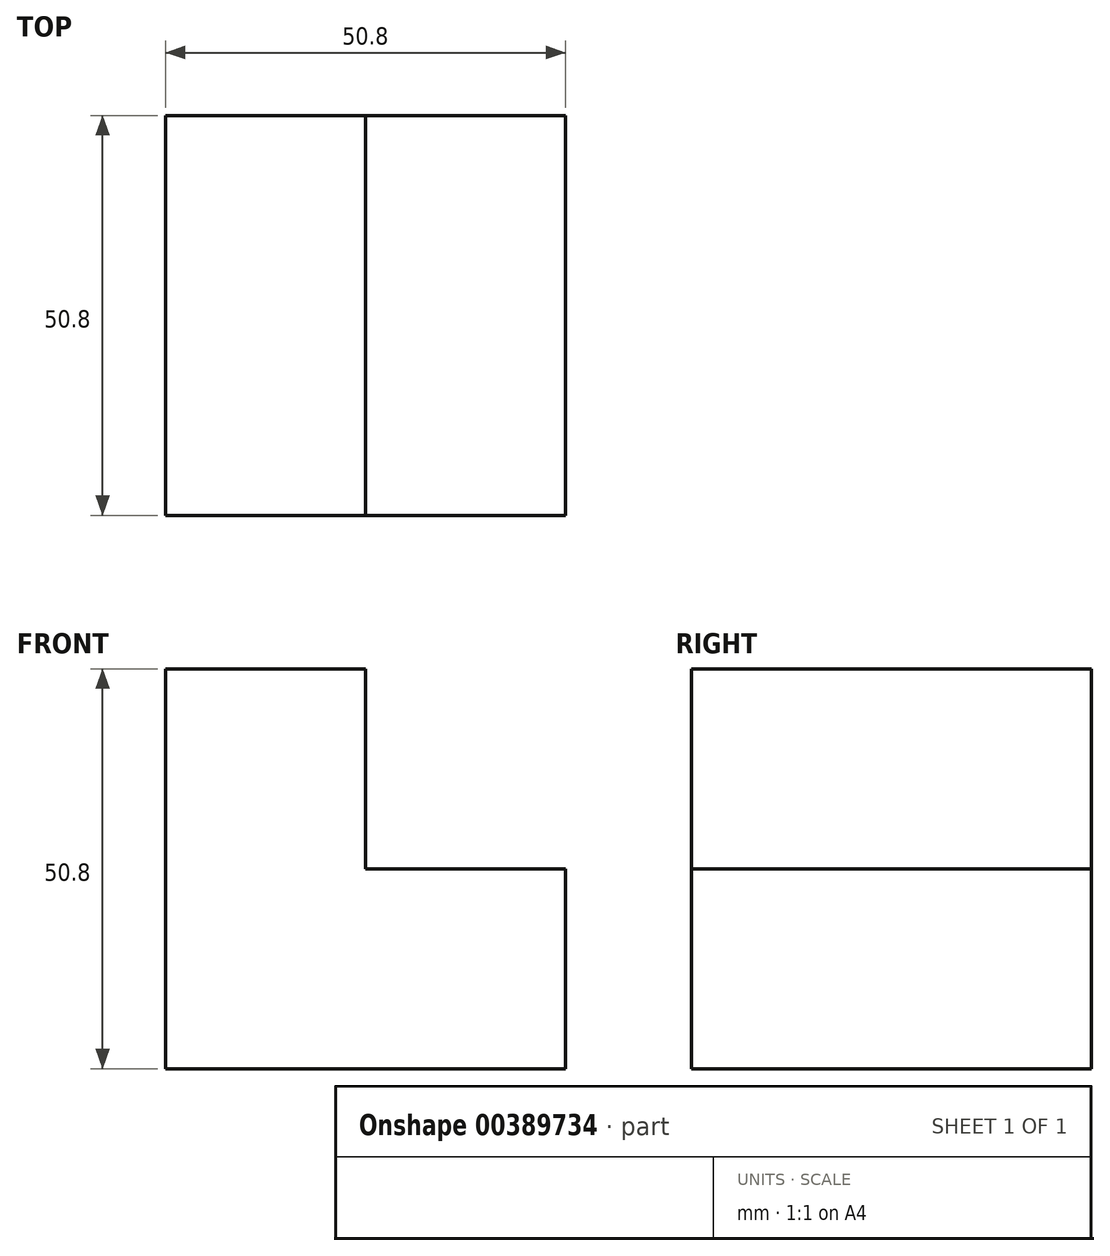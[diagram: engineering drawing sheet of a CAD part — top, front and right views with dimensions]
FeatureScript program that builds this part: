
annotation { "Feature Type Name" : "Feature", "Feature Type Description" : "" }
export const myFeature = defineFeature(function(context is Context, id is Id, definition is map)
    precondition{}
    {
        {
            var Q0;
            Q0=qCreatedBy(makeId("Front.planeOp"),FACE);
            var sketch = newSketch(context, id + "F0", { "sketchPlane" : qUnion([Q0])});
            skLineSegment(sketch, "E0.bottom", {"start": v(0, 0) * mm, "end": v(25.4, 0) * mm});
            skLineSegment(sketch, "E0.top", {"start": v(0, 25.4) * mm, "end": v(25.4, 25.4) * mm});
            skLineSegment(sketch, "E0.left", {"start": v(0, 0) * mm, "end": v(0, 25.4) * mm});
            skLineSegment(sketch, "E0.right", {"start": v(25.4, 0) * mm, "end": v(25.4, 25.4) * mm});
            skLineSegment(sketch, "E1.top", {"start": v(0, 50.8) * mm, "end": v(25.4, 50.8) * mm});
            skLineSegment(sketch, "E1.left", {"start": v(0, 25.4) * mm, "end": v(0, 50.8) * mm});
            skLineSegment(sketch, "E1.right", {"start": v(25.4, 25.4) * mm, "end": v(25.4, 50.8) * mm});
            skLineSegment(sketch, "E2.bottom", {"start": v(25.4, 25.4) * mm, "end": v(50.8, 25.4) * mm});
            skLineSegment(sketch, "E2.top", {"start": v(25.4, 0) * mm, "end": v(50.8, 0) * mm});
            skLineSegment(sketch, "E2.left", {"start": v(25.4, 25.4) * mm, "end": v(25.4, 0) * mm});
            skLineSegment(sketch, "E2.right", {"start": v(50.8, 25.4) * mm, "end": v(50.8, 0) * mm});
            skSolve(sketch);
        }
        {
            var Q0;
            Q0=makeQuery(id+"F0.imprint","IMPRINT",FACE,{"disambiguationData":[TD([[makeQuery(id+"F0.imprint","IMPRINT",EDGE,{"derivedFrom":sQuery(id+"F0.wireOp",EDGE,"E0.top")}),1.0]])]});
            var Q1;
            Q1=makeQuery(id+"F0.imprint","IMPRINT",FACE,{"disambiguationData":[TD([[makeQuery(id+"F0.imprint","IMPRINT",EDGE,{"derivedFrom":sQuery(id+"F0.wireOp",EDGE,"E0.bottom")}),1.0]])]});
            var Q2;
            Q2=makeQuery(id+"F0.imprint","IMPRINT",FACE,{"disambiguationData":[TD([[makeQuery(id+"F0.imprint","IMPRINT",EDGE,{"derivedFrom":sQuery(id+"F0.wireOp",EDGE,"E2.bottom")}),-1.0]])]});
            extrude(context, id + "F1", {"entities" : qUnion([Q0, Q1, Q2]), "depth" : 50.8 * mm, "offsetDistance" : 25.4 * mm});
        }
    });
